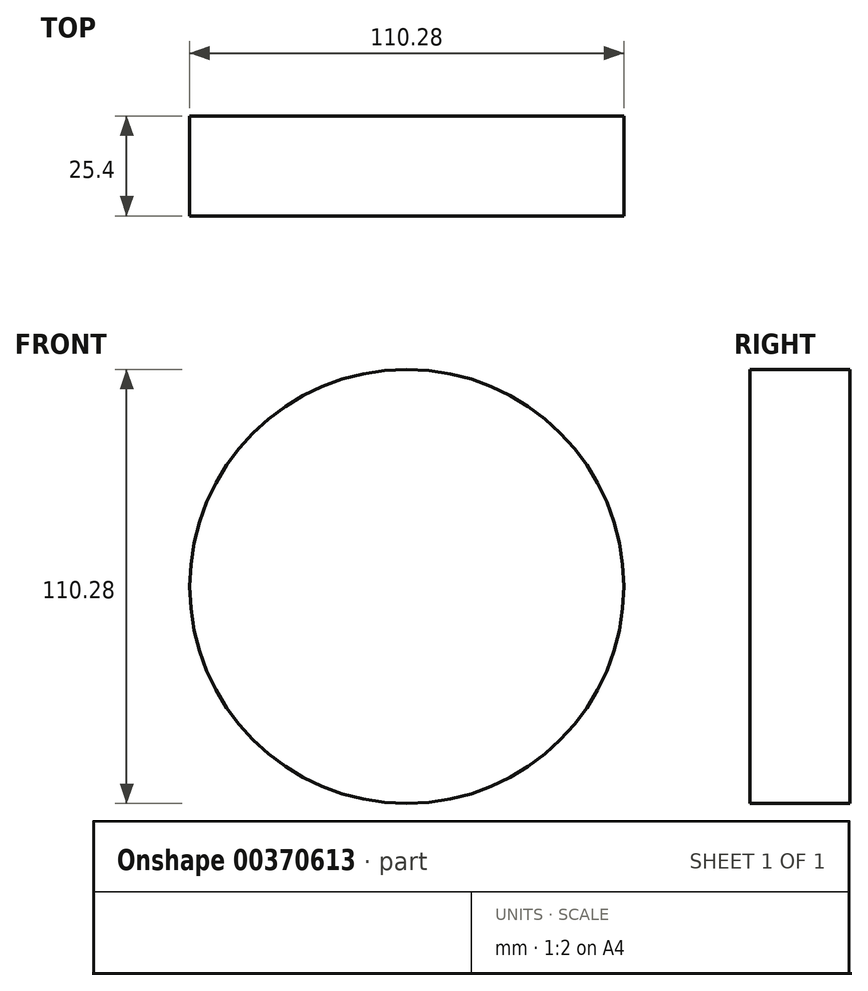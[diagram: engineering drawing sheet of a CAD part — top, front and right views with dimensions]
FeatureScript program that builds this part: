
annotation { "Feature Type Name" : "Feature", "Feature Type Description" : "" }
export const myFeature = defineFeature(function(context is Context, id is Id, definition is map)
    precondition{}
    {
        {
            var Q0;
            Q0=qCreatedBy(makeId("Front.planeOp"),FACE);
            var sketch = newSketch(context, id + "F0", { "sketchPlane" : qUnion([Q0])});
            skCircle(sketch, "E0", {"center": v(0, 0) * mm, "radius": 55.14 * mm});
            skSolve(sketch);
        }
        {
            var Q0;
            Q0=makeQuery(id+"F0.imprint","IMPRINT",FACE,{"disambiguationData":[TD([[makeQuery(id+"F0.imprint","IMPRINT",EDGE,{"derivedFrom":sQuery(id+"F0.wireOp",EDGE,"E0")}),1.0]])]});
            extrude(context, id + "F1", {"entities" : qUnion([Q0]), "depth" : 25.4 * mm});
        }
        {
            var Q0;
            Q0=qCreatedBy(makeId("Front.planeOp"),FACE);
            var sketch = newSketch(context, id + "F2", { "sketchPlane" : qUnion([Q0])});
            skLineSegment(sketch, "E1.bottom", {"start": v(-19.19, 19.55) * mm, "end": v(22.08, 19.55) * mm});
            skLineSegment(sketch, "E1.top", {"start": v(-19.19, -22.63) * mm, "end": v(22.08, -22.63) * mm});
            skLineSegment(sketch, "E1.left", {"start": v(-19.19, 19.55) * mm, "end": v(-19.19, -22.63) * mm});
            skLineSegment(sketch, "E1.right", {"start": v(22.08, 19.55) * mm, "end": v(22.08, -22.63) * mm});
            skSolve(sketch);
        }
        {
            var Q0;
            Q0 = qSketchRegion(id + "F2", true);
            extrude(context, id + "F3", {"entities" : qUnion([Q0]), "operationType" : NewBodyOperationType.ADD, "depth" : 25.4 * mm});
        }
    });
